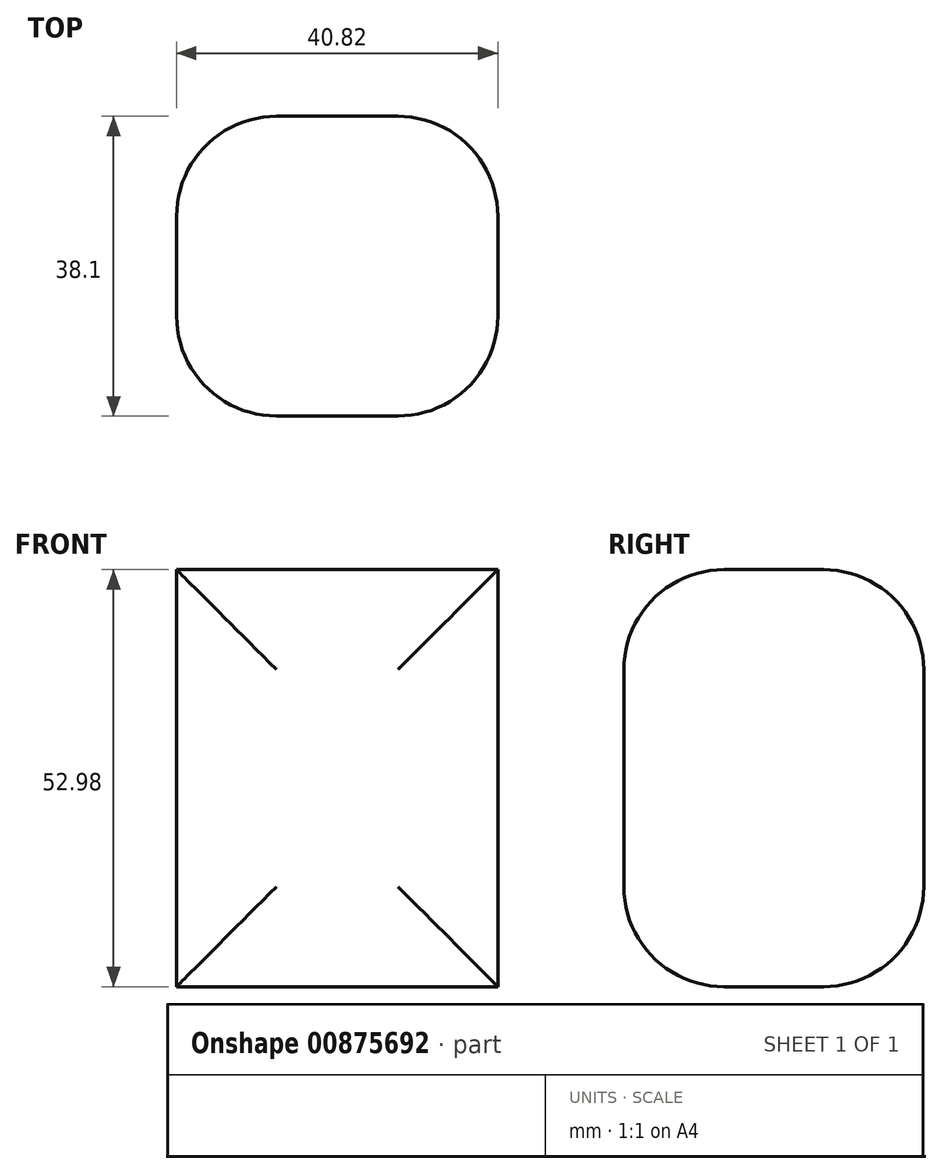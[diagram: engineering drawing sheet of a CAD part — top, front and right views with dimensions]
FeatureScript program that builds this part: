
annotation { "Feature Type Name" : "Feature", "Feature Type Description" : "" }
export const myFeature = defineFeature(function(context is Context, id is Id, definition is map)
    precondition{}
    {
        {
            var Q0;
            Q0=qCreatedBy(makeId("Front.planeOp"),FACE);
            var sketch = newSketch(context, id + "F0", { "sketchPlane" : qUnion([Q0])});
            skLineSegment(sketch, "E0.bottom", {"start": v(17.75, 13.88) * mm, "end": v(58.57, 13.88) * mm});
            skLineSegment(sketch, "E0.top", {"start": v(17.75, 66.86) * mm, "end": v(58.57, 66.86) * mm});
            skLineSegment(sketch, "E0.left", {"start": v(17.75, 13.88) * mm, "end": v(17.75, 66.86) * mm});
            skLineSegment(sketch, "E0.right", {"start": v(58.57, 13.88) * mm, "end": v(58.57, 66.86) * mm});
            skSolve(sketch);
        }
        {
            var Q0;
            Q0 = qSketchRegion(id + "F0", true);
            extrude(context, id + "F1", {"entities" : qUnion([Q0]), "endBound" : BoundingType.SYMMETRIC, "depth" : 38.1 * mm, "offsetDistance" : 25.4 * mm});
        }
        {
            var Q0;
            Q0=makeQuery(id+"F1.opExtrude","CAP_FACE",FACE,{"disambiguationData":[OSD([sQuery(id+"F0.wireOp",EDGE,"E0.bottom"),sQuery(id+"F0.wireOp",EDGE,"E0.top"),sQuery(id+"F0.wireOp",EDGE,"E0.left"),sQuery(id+"F0.wireOp",EDGE,"E0.right")])],"isStart":true});
            var Q1;
            Q1=makeQuery(id+"F1.opExtrude","CAP_FACE",FACE,{"disambiguationData":[OSD([sQuery(id+"F0.wireOp",EDGE,"E0.bottom"),sQuery(id+"F0.wireOp",EDGE,"E0.top"),sQuery(id+"F0.wireOp",EDGE,"E0.left"),sQuery(id+"F0.wireOp",EDGE,"E0.right")])],"isStart":false});
            fillet(context, id + "F2", {"entities" : qUnion([Q0, Q1]), "radius" : 12.7 * mm, "tangentPropagation" : true, "allowEdgeOverflow" : false});
        }
    });
